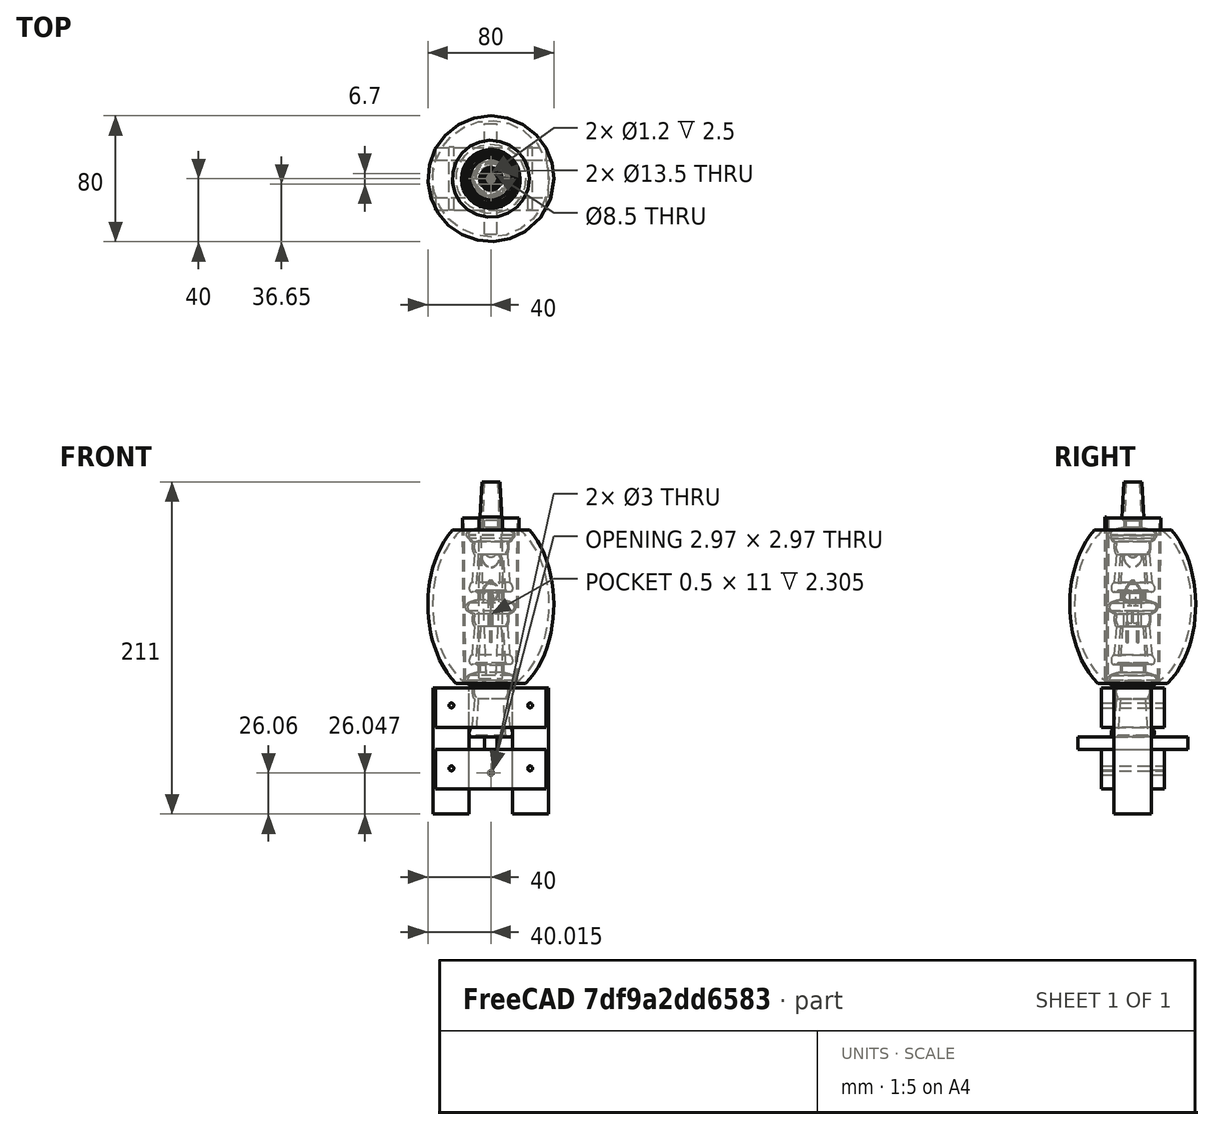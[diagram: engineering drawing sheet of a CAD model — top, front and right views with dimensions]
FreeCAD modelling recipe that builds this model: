
FCSTD DOCUMENT  (FreeCAD 0.17R13519 (Git))
Label: Atadam_Vaporizer_v1.0.0
License: All rights reserved
LicenseURL: http://en.wikipedia.org/wiki/All_rights_reserved
objects: Part::Fuse×25, Part::Cylinder×17, Part::Box×15, Part::Part2DObjectPython×14, Part::Cut×13, Part::MultiCommon×4, Part::Ellipsoid×4, Part::Loft×3, App::DocumentObjectGroup×3, Part::MultiFuse×2, Part::Sweep×2, Part::Cone×2, Part::Ellipse×2, Part::Extrusion×2, Part::Torus×2, Part::Helix×1, Part::Wedge×1
note: 109 computed .brp shape members not serialized (recipe doc carries the construction recipe); baked Part::Feature solids carry a one-line shape summary decoded from their .brp

FEATURE [Part::Part2DObjectPython] Circle003  # Draft 2D object (typed FeaturePython)
  FirstAngle = 0
  LastAngle = 0
  MakeFace = false
  Placement = pos=(0,0,91) rot=(0,0,1;0rad)
  Radius = 2
FEATURE [Part::Part2DObjectPython] Circle  # Draft 2D object (typed FeaturePython)
  FirstAngle = 0
  LastAngle = 0
  MakeFace = false
  Placement = pos=(0,0,91) rot=(0,0,1;0rad)
  Radius = 3
FEATURE [Part::Helix] Helix  label="halogen helix"
  Angle = 0
  AttacherType = Attacher::AttachEngine3D
  Height = 3.5
  LocalCoord = 0
  Pitch = 0.28
  Placement = pos=(0,0,89) rot=(0,0,1;1.5708rad)
  Radius = 0.75
  Style = 1
FEATURE [Part::Cylinder] Cylinder014
  Angle = 360
  AttacherType = Attacher::AttachEngine3D
  Height = 13
  Placement = pos=(0,-3.35,54) rot=(0,0,1;0rad)
  Radius = 0.6
FEATURE [Part::Box] Box006  label="Cube005"
  AttacherType = Attacher::AttachEngine3D
  Height = 11
  Length = 0.5
  Placement = pos=(-0.25,-3.5,66.5) rot=(0,0,1;0rad)
  Width = 3
FEATURE [Part::Cylinder] Cylinder013
  Angle = 360
  AttacherType = Attacher::AttachEngine3D
  Height = 13
  Placement = pos=(0,3.35,54) rot=(0,0,1;0rad)
  Radius = 0.6
FEATURE [Part::Box] Box005  label="Cube004"
  AttacherType = Attacher::AttachEngine3D
  Height = 11
  Length = 0.5
  Placement = pos=(-0.25,0.5,66.5) rot=(0,0,1;0rad)
  Width = 3
FEATURE [Part::Cylinder] Cylinder012
  Angle = 360
  AttacherType = Attacher::AttachEngine3D
  Height = 13
  Placement = pos=(0,-3.35,54) rot=(0,0,1;0rad)
  Radius = 0.6
FEATURE [Part::Box] Box004  label="Cube003"
  AttacherType = Attacher::AttachEngine3D
  Height = 11
  Length = 0.5
  Placement = pos=(-0.25,-3.5,66.5) rot=(0,0,1;0rad)
  Width = 3
FEATURE [Part::Box] Box003  label="halogen-cube"
  AttacherType = Attacher::AttachEngine3D
  Height = 15.5
  Length = 3
  Placement = pos=(-1.5,-5.5,64.5) rot=(0,0,1;0rad)
  Width = 11
FEATURE [Part::Cylinder] Cylinder015
  Angle = 360
  AttacherType = Attacher::AttachEngine3D
  Height = 13
  Placement = pos=(0,3.35,54) rot=(0,0,1;0rad)
  Radius = 0.6
FEATURE [Part::Box] Box007  label="Cube006"
  AttacherType = Attacher::AttachEngine3D
  Height = 11
  Length = 0.5
  Placement = pos=(-0.25,0.5,66.5) rot=(0,0,1;0rad)
  Width = 3
FEATURE [Part::Part2DObjectPython] Circle008  # Draft 2D object (typed FeaturePython)
  FirstAngle = 0
  LastAngle = 0
  MakeFace = false
  Placement = pos=(0,1.75,77.5) rot=(0,0,1;0rad)
  Radius = 0.05
FEATURE [Part::Part2DObjectPython] Circle004  # Draft 2D object (typed FeaturePython)
  FirstAngle = 0
  LastAngle = 0
  MakeFace = false
  Placement = pos=(0,0,86) rot=(0,0,1;0rad)
  Radius = 4.5
FEATURE [Part::Part2DObjectPython] Line001  # Draft 2D object (typed FeaturePython)
  ChamferSize = 0
  Closed = false
  End = (0,-1.75,86.5)
  FilletRadius = 0
  Length = 9
  MakeFace = true
  Placement = pos=(0,-1,0) rot=(0,0,1;0rad)
  Points = (2) [(0,-0.75,77.5),(0,-0.75,86.5)]
  Start = (0,-1.75,77.5)
  Subdivisions = 0
FEATURE [Part::Part2DObjectPython] Line002  # Draft 2D object (typed FeaturePython)
  ChamferSize = 0
  Closed = false
  End = (0,1.75,83)
  FilletRadius = 0
  Length = 1
  MakeFace = true
  Points = (2) [(-8.9407e-08,0.75,83),(0,1.75,83)]
  Start = (-8.9407e-08,0.75,83)
  Subdivisions = 0
FEATURE [Part::Part2DObjectPython] Circle002  label="Circle001"  # Draft 2D object (typed FeaturePython)
  FirstAngle = 0
  LastAngle = 0
  MakeFace = false
  Placement = pos=(0,0,86) rot=(0,0,1;0rad)
  Radius = 5.5
FEATURE [Part::Part2DObjectPython] Rectangle  # Draft 2D object (typed FeaturePython)
  ChamferSize = 0
  Columns = 1
  FilletRadius = 0
  Height = 11
  Length = 3
  MakeFace = false
  Placement = pos=(-1.5,-5.5,80) rot=(0,0,1;0rad)
  Rows = 1
FEATURE [Part::Loft] Loft001
  Closed = false
  MaxDegree = 5
  Ruled = false
  Sections = -> [Rectangle,Circle002,Circle]
  Solid = true
FEATURE [Part::Part2DObjectPython] Circle006  # Draft 2D object (typed FeaturePython)
  FirstAngle = 0
  LastAngle = 0
  MakeFace = false
  Placement = pos=(0,0,91.3) rot=(0.573962,0.584068,0.573962;0.030142rad)
  Radius = 2.4
FEATURE [Part::Part2DObjectPython] Line  # Draft 2D object (typed FeaturePython)
  ChamferSize = 0
  Closed = false
  End = (0,1.75,77.5)
  FilletRadius = 0
  Length = 5.5
  MakeFace = true
  Placement = pos=(0,1,0) rot=(0,0,1;0rad)
  Points = (2) [(0,0.75,83),(0,0.75,77.5)]
  Start = (0,1.75,83)
  Subdivisions = 0
FEATURE [Part::Part2DObjectPython] Rectangle001  # Draft 2D object (typed FeaturePython)
  ChamferSize = 0
  Columns = 1
  FilletRadius = 0
  Height = 9
  Length = 1
  MakeFace = false
  Placement = pos=(-0.5,-4.5,80) rot=(0,0,1;0rad)
  Rows = 1
FEATURE [Part::Loft] Loft
  Closed = false
  MaxDegree = 5
  Ruled = false
  Sections = -> [Rectangle001,Circle004,Circle003]
  Solid = true
FEATURE [Part::Part2DObjectPython] Line003  # Draft 2D object (typed FeaturePython)
  ChamferSize = 0
  Closed = false
  End = (8.9407e-08,-0.75,86.5)
  FilletRadius = 0
  Length = 1
  MakeFace = true
  Points = (2) [(0,-1.75,86.5),(8.9407e-08,-0.75,86.5)]
  Start = (0,-1.75,86.5)
  Subdivisions = 0
FEATURE [Part::Part2DObjectPython] Circle007  # Draft 2D object (typed FeaturePython)
  FirstAngle = 0
  LastAngle = 0
  MakeFace = false
  Placement = pos=(0,-1.75,77.5) rot=(0,0,1;0rad)
  Radius = 0.05
FEATURE [Part::Part2DObjectPython] Circle005  # Draft 2D object (typed FeaturePython)
  FirstAngle = 0
  LastAngle = 0
  MakeFace = false
  Placement = pos=(0,0,93.5) rot=(0,0,1;0rad)
  Radius = 1
FEATURE [Part::Loft] Loft002  label="halogen-cap"
  Closed = false
  MaxDegree = 5
  Ruled = false
  Sections = -> [Circle,Circle006,Circle005]
  Solid = true
FEATURE [Part::MultiFuse] Fusion006
  Shapes = -> [Line001,Line,Line003,Line002]
FEATURE [Part::Sweep] Sweep
  Frenet = false
  Sections = -> [Circle007]
  Solid = true
  Spine = -> Fusion006 [Edge1]
  Transition = 1
FEATURE [Part::Sweep] Sweep001
  Frenet = false
  Sections = -> [Circle008]
  Solid = true
  Spine = -> Fusion006 [Edge2]
  Transition = 1
FEATURE [Part::Fuse] Fusion017
  Base = -> Cylinder014
  Tool = -> Cylinder015
FEATURE [Part::Cut] Cut015  label="halogen-mid-glass"
  Base = -> Loft001
  Tool = -> Loft
FEATURE [Part::Fuse] Fusion008
  Base = -> Box004
  Tool = -> Box005
FEATURE [Part::Fuse] Fusion010
  Base = -> Sweep
  Tool = -> Sweep001
FEATURE [Part::Fuse] Fusion013
  Base = -> Cut015
  Tool = -> Loft002
FEATURE [Part::Fuse] Fusion007
  Base = -> Cylinder012
  Tool = -> Cylinder013
FEATURE [Part::Fuse] Fusion009
  Base = -> Fusion007
  Tool = -> Fusion008
FEATURE [Part::Cut] Cut016  label="halogen-glass-bottom"
  Base = -> Box003
  Tool = -> Fusion009
FEATURE [Part::Fuse] Fusion014  label="halogen-glass"
  Base = -> Cut016
  Placement = pos=(0,0,6) rot=(0,0,1;0rad)
  Tool = -> Fusion013
FEATURE [Part::Fuse] Fusion016
  Base = -> Box006
  Tool = -> Box007
FEATURE [Part::Fuse] Fusion015
  Base = -> Fusion017
  Tool = -> Fusion016
FEATURE [Part::Fuse] Fusion012  label="hologen-metals"
  Base = -> Fusion015
  Placement = pos=(0,0,6) rot=(0,0,1;0rad)
  Tool = -> Fusion010
FEATURE [Part::MultiCommon] Common  label="19F-14M"
  Placement = pos=(0,0,92) rot=(0,0,1;0rad)
FEATURE [Part::MultiCommon] Common002  label="19F-19M001"
  Placement = pos=(0,0,46) rot=(0,0,1;0rad)
FEATURE [Part::Ellipsoid] Ellipsoid
  Angle1 = -90
  Angle2 = 90
  Angle3 = 360
  AttacherType = Attacher::AttachEngine3D
  Radius1 = 60
  Radius2 = 40
  Radius3 = 40
FEATURE [Part::Ellipsoid] Ellipsoid001
  Angle1 = -90
  Angle2 = 90
  Angle3 = 360
  AttacherType = Attacher::AttachEngine3D
  Radius1 = 55
  Radius2 = 37
  Radius3 = 37
FEATURE [Part::Cut] Cut
  Base = -> Ellipsoid
  Tool = -> Ellipsoid001
FEATURE [Part::Cylinder] Cylinder
  Angle = 360
  AttacherType = Attacher::AttachEngine3D
  Height = 97.5
  Placement = pos=(0,0,-50) rot=(0,0,1;0rad)
  Radius = 70
FEATURE [Part::MultiCommon] Common003  label="Coconut"
  Placement = pos=(0,0,84) rot=(0,0,1;0rad)
  Shapes = -> [Cut,Cylinder]
FEATURE [Part::MultiCommon] Common004  label="19F-19M"
FEATURE [Part::Cone] Cone
  Angle = 360
  AttacherType = Attacher::AttachEngine3D
  Height = 103
  Radius1 = 16
  Radius2 = 17
FEATURE [Part::Cone] Cone001
  Angle = 360
  AttacherType = Attacher::AttachEngine3D
  Height = 103
  Radius1 = 17
  Radius2 = 18
FEATURE [Part::Cut] Cut017  label="Reflector-Conic"
  Base = -> Cone001
  Placement = pos=(0,0,36) rot=(0,0,1;0rad)
  Tool = -> Cone
FEATURE [Part::Box] Box008  label="Reflector-Strip"
  AttacherType = Attacher::AttachEngine3D
  Height = 102.5
  Length = 15
  Placement = pos=(-7.5,-17.8,37.2) rot=(0,0,1;0rad)
  Width = 1
FEATURE [Part::Wedge] Wedge  label="Reflector-Wedge"
  AttacherType = Attacher::AttachEngine3D
  Placement = pos=(0,-18,139) rot=(-0.999924,-0.008726,0.008726;1.57087rad)
  X2max = 3
  X2min = -3
  Xmax = 7
  Xmin = -7
  Ymax = 103
  Ymin = 0
  Z2max = 3
  Z2min = -1
  Zmax = 3
  Zmin = -1
FEATURE [Part::Cut] Cut018  label="Reflector-C"
  Base = -> Cut017
  Tool = -> Wedge
FEATURE [Part::Cut] Cut019  label="Coconut-Notched"
  Base = -> Common003
  Tool = -> Box008
FEATURE [Part::Fuse] Fusion  label="Reflector-430"
  Base = -> Box008
  Tool = -> Cut018
FEATURE [App::DocumentObjectGroup] Group  label="Halogen"
  Group = -> [Fusion012,Fusion014,Fusion006,Helix]
FEATURE [Part::Box] Box  label="Wood001"
  AttacherType = Attacher::AttachEngine3D
  Height = 25
  Length = 8
  Placement = pos=(-35,-11.94,6) rot=(0,0,-1;1.5708rad)
  Width = 70
FEATURE [Part::Box] Box009  label="Wood002"
  AttacherType = Attacher::AttachEngine3D
  Height = 25
  Length = 8
  Placement = pos=(-35,19.94,6) rot=(0,0,-1;1.5708rad)
  Width = 70
FEATURE [Part::Box] Box010  label="Wood003"
  AttacherType = Attacher::AttachEngine3D
  Height = 25
  Length = 8
  Placement = pos=(-35,-11.94,-33) rot=(0,0,-1;1.5708rad)
  Width = 70
FEATURE [Part::Box] Box011  label="Wood004"
  AttacherType = Attacher::AttachEngine3D
  Height = 25
  Length = 8
  Placement = pos=(-35,19.94,-33) rot=(0,0,-1;1.5708rad)
  Width = 70
FEATURE [Part::Box] Box012  label="Cork002"
  AttacherType = Attacher::AttachEngine3D
  Height = 80
  Length = 23
  Placement = pos=(13.79,-11.94,-49) rot=(0,0,1;0rad)
  Width = 23.88
FEATURE [Part::Fuse] Fusion019  label="Wood-Up"
  Base = -> Box
  Tool = -> Box009
FEATURE [Part::Fuse] Fusion020  label="Wood-Down"
  Base = -> Box010
  Tool = -> Box011
FEATURE [Part::Fuse] Fusion021  label="Wood"
  Base = -> Fusion019
  Tool = -> Fusion020
FEATURE [App::DocumentObjectGroup] Group001  label="GonG"
  Group = -> [Common,Common002,Common004]
FEATURE [Part::Cylinder] Cylinder016  label="Bolt001"
  Angle = 360
  AttacherType = Attacher::AttachEngine3D
  Height = 40
  Placement = pos=(-25,-20,20) rot=(-1,0,0;1.5708rad)
  Radius = 1.5
FEATURE [Part::Cylinder] Cylinder017  label="Bolt002"
  Angle = 360
  AttacherType = Attacher::AttachEngine3D
  Height = 40
  Placement = pos=(25,-20,20) rot=(-1,0,0;1.5708rad)
  Radius = 1.5
FEATURE [Part::Cylinder] Cylinder018  label="Bolt003"
  Angle = 360
  AttacherType = Attacher::AttachEngine3D
  Height = 40
  Placement = pos=(-25,-20,-20) rot=(-1,0,0;1.5708rad)
  Radius = 1.5
FEATURE [Part::Cylinder] Cylinder019  label="Bolt004"
  Angle = 360
  AttacherType = Attacher::AttachEngine3D
  Height = 40
  Placement = pos=(25,-20,-20) rot=(-1,0,0;1.5708rad)
  Radius = 1.5
FEATURE [Part::Fuse] Fusion022  label="Bolt-Up"
  Base = -> Cylinder016
  Tool = -> Cylinder017
FEATURE [Part::Fuse] Fusion023  label="Bolt-Down"
  Base = -> Cylinder018
  Tool = -> Cylinder019
FEATURE [Part::Fuse] Fusion024  label="Bolt"
  Base = -> Fusion022
  Tool = -> Fusion023
FEATURE [Part::Ellipse] Ellipse
  Angle0 = 0
  Angle1 = 360
  AttacherType = Attacher::AttachEngine3D
  MajorRadius = 3.5
  MinorRadius = 3
  Placement = pos=(6,0,1) rot=(0.573962,0.584068,0.573962;2.08435rad)
FEATURE [Part::Ellipse] Ellipse001
  Angle0 = 0
  Angle1 = 360
  AttacherType = Attacher::AttachEngine3D
  MajorRadius = 3.5
  MinorRadius = 3
  Placement = pos=(6,0,1) rot=(0.573962,0.584068,0.573962;2.08435rad)
FEATURE [Part::Cylinder] Cylinder006
  Angle = 360
  AttacherType = Attacher::AttachEngine3D
  Height = 15
  Radius = 8
FEATURE [Part::Extrusion] Extrude
  Base = -> Ellipse
  Dir = (1,0,0)
  DirMode = 0
  FaceMakerClass = Part::FaceMakerBullseye
  LengthFwd = 20
  LengthRev = 0
  Placement = pos=(-15,0,0) rot=(0,0,1;0rad)
  Solid = true
  Symmetric = false
FEATURE [Part::Extrusion] Extrude001
  Base = -> Ellipse001
  Dir = (1,0,0)
  DirMode = 0
  FaceMakerClass = Part::FaceMakerBullseye
  LengthFwd = 20
  LengthRev = 0
  Placement = pos=(0,-15,0) rot=(0,0,1;1.5708rad)
  Solid = true
  Symmetric = false
FEATURE [Part::Ellipsoid] Ellipsoid002
  Angle1 = -90
  Angle2 = 90
  Angle3 = 360
  AttacherType = Attacher::AttachEngine3D
  Radius1 = 10.5
  Radius2 = 6.6
  Radius3 = 6.6
FEATURE [Part::Ellipsoid] Ellipsoid003
  Angle1 = -90
  Angle2 = 90
  Angle3 = 360
  AttacherType = Attacher::AttachEngine3D
  Radius1 = 10.2
  Radius2 = 6.3
  Radius3 = 6.3
FEATURE [Part::Cut] Cut005
  Base = -> Ellipsoid002
  Placement = pos=(0,0,2) rot=(0,0,1;0rad)
  Tool = -> Ellipsoid003
FEATURE [Part::Cut] Cut006
  Base = -> Cut005
  Tool = -> Cylinder006
FEATURE [Part::Cut] Cut007
  Base = -> Cut006
  Tool = -> Extrude
FEATURE [Part::Cut] Cut008  label="filter-cheap"
  Base = -> Cut007
  Placement = pos=(0,0,116) rot=(0,0,1;0rad)
  Tool = -> Extrude001
FEATURE [Part::Torus] Torus  label="316-Bent001"
  Angle1 = -180
  Angle2 = 180
  Angle3 = 90
  AttacherType = Attacher::AttachEngine3D
  Placement = pos=(0,-11.94,-15) rot=(0,1,0;1.5708rad)
  Radius1 = 7.94
  Radius2 = 1.5
FEATURE [Part::Torus] Torus001  label="316-Bent002"
  Angle1 = -180
  Angle2 = 180
  Angle3 = 90
  AttacherType = Attacher::AttachEngine3D
  Placement = pos=(0,11.94,-15) rot=(0.707107,0,-0.707107;3.14159rad)
  Radius1 = 7.94
  Radius2 = 1.5
FEATURE [Part::Cylinder] Cylinder001
  Angle = 360
  AttacherType = Attacher::AttachEngine3D
  Height = 79
  Placement = pos=(0,-4,-21) rot=(0,0,1;0rad)
  Radius = 1.5
FEATURE [Part::Cylinder] Cylinder002
  Angle = 360
  AttacherType = Attacher::AttachEngine3D
  Height = 79
  Placement = pos=(0,4,-21) rot=(0,0,1;0rad)
  Radius = 1.5
FEATURE [Part::Cylinder] Cylinder003
  Angle = 360
  AttacherType = Attacher::AttachEngine3D
  Height = 10
  Placement = pos=(0,-3.3,48) rot=(0,0,1;0rad)
  Radius = 0.65
FEATURE [Part::Cylinder] Cylinder004
  Angle = 360
  AttacherType = Attacher::AttachEngine3D
  Height = 10
  Placement = pos=(0,3.3,48) rot=(0,0,1;0rad)
  Radius = 0.65
FEATURE [Part::Box] Box001  label="Cube"
  AttacherType = Attacher::AttachEngine3D
  Height = 10
  Length = 0.7
  Placement = pos=(-0.35,2.5,48) rot=(0,0,1;0rad)
  Width = 0.4
FEATURE [Part::Box] Box002  label="Cube001"
  AttacherType = Attacher::AttachEngine3D
  Height = 10
  Length = 0.7
  Placement = pos=(-0.35,-2.9,48) rot=(0,0,1;0rad)
  Width = 0.4
FEATURE [Part::Fuse] Fusion003
  Base = -> Cylinder004
  Tool = -> Box001
FEATURE [Part::Cut] Cut012  label="316-Grooved002"
  Base = -> Cylinder002
  Tool = -> Fusion003
FEATURE [Part::Fuse] Fusion004
  Base = -> Cylinder003
  Tool = -> Box002
FEATURE [Part::Cut] Cut011  label="316-Grooved001"
  Base = -> Cylinder001
  Tool = -> Fusion004
FEATURE [Part::Fuse] Fusion025  label="316-Grooved"
  Base = -> Cut011
  Placement = pos=(0,0,6) rot=(0,0,1;0rad)
  Tool = -> Cut012
FEATURE [Part::Cylinder] Cylinder020  label="316-Terminal001"
  Angle = 360
  AttacherType = Attacher::AttachEngine3D
  Height = 20
  Placement = pos=(0,-11.94,-22.94) rot=(0.999924,0.008726,-0.008726;1.57087rad)
  Radius = 1.5
FEATURE [Part::Box] Box013  label="Cork001"
  AttacherType = Attacher::AttachEngine3D
  Height = 80
  Length = 23
  Placement = pos=(-36.79,-11.94,-49) rot=(0,0,1;0rad)
  Width = 23.88
FEATURE [Part::Cylinder] Cylinder011  label="filter-big"
  Angle = 360
  AttacherType = Attacher::AttachEngine3D
  Height = 0.3
  Placement = pos=(0,0,128) rot=(0,0,1;0rad)
  Radius = 13.5
FEATURE [Part::Cylinder] Cylinder021  label="316-Terminal002"
  Angle = 360
  AttacherType = Attacher::AttachEngine3D
  Height = 20
  Placement = pos=(0,31.94,-22.94) rot=(0.999924,0.008726,-0.008726;1.57087rad)
  Radius = 1.5
FEATURE [Part::Box] Box014  label="Wood005"
  AttacherType = Attacher::AttachEngine3D
  Height = 8
  Length = 8
  Placement = pos=(-4,-35,-8) rot=(0,0,1;0rad)
  Width = 70
FEATURE [Part::Fuse] Fusion026  label="316-Terminal"
  Base = -> Cylinder020
  Tool = -> Cylinder021
FEATURE [Part::Fuse] Fusion027  label="316-Bent"
  Base = -> Torus
  Tool = -> Torus001
FEATURE [Part::Fuse] Fusion028  label="316-Bottom"
  Base = -> Fusion026
  Tool = -> Fusion027
FEATURE [Part::Fuse] Fusion029  label="316"
  Base = -> Fusion025
  Tool = -> Fusion028
FEATURE [Part::Fuse] Fusion030  label="Cork"
  Base = -> Box012
  Tool = -> Box013
FEATURE [App::DocumentObjectGroup] Group002  label="Filter"
  Group = -> [Cylinder011,Cut008]
FEATURE [Part::MultiFuse] Fusion031  label="Wood-Down001"
  Shapes = -> [Box010,Box011]
FEATURE [Part::Cut] Cut020  label="Wood-Down002"
  Base = -> Fusion031
  Tool = -> Fusion029
